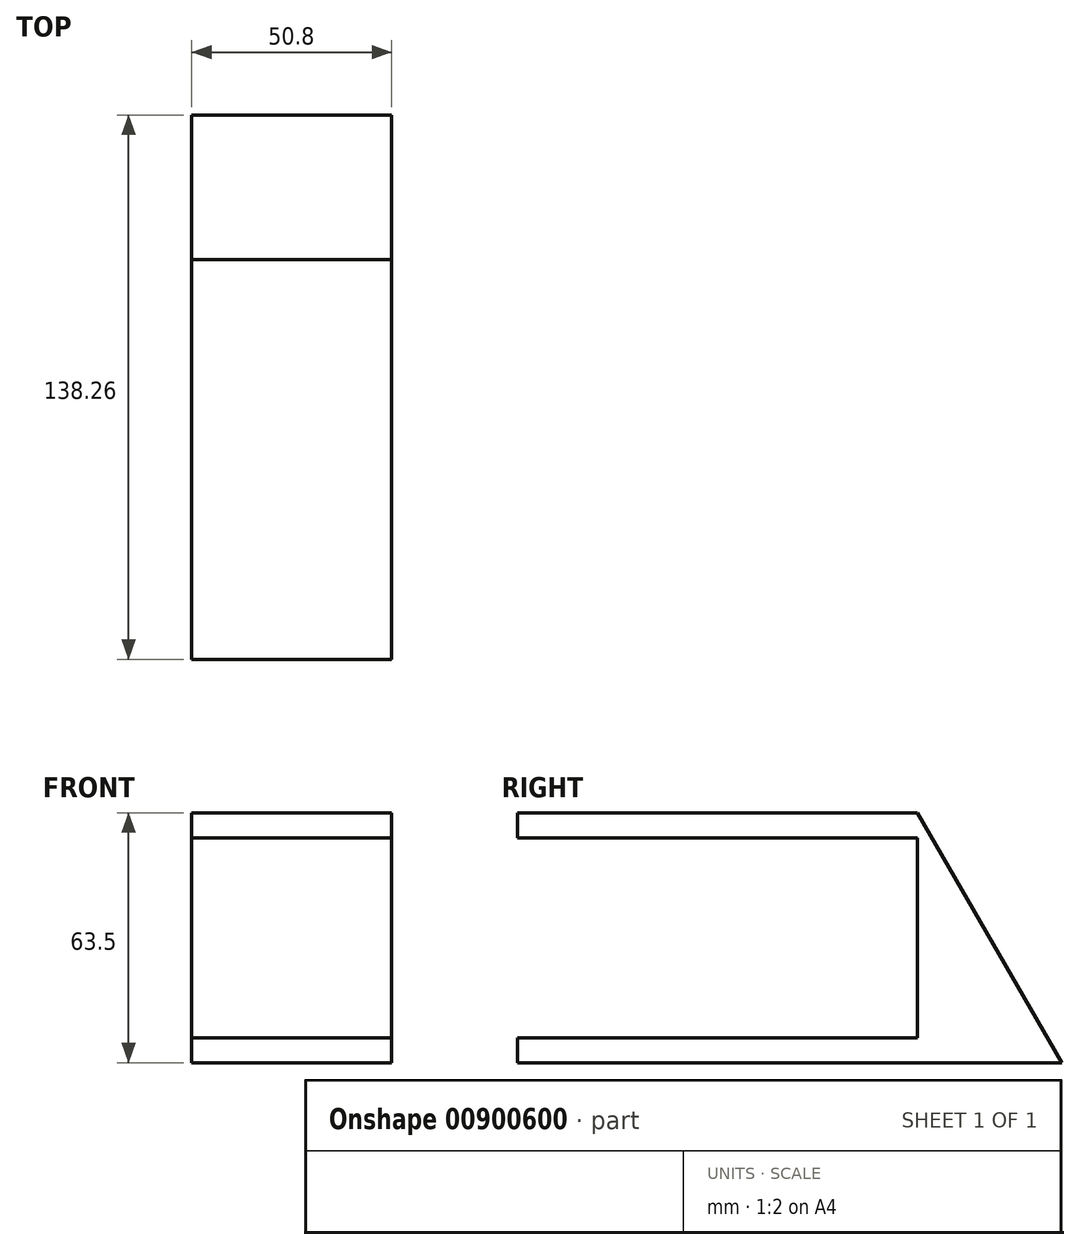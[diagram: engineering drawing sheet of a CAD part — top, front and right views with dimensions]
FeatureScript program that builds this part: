
annotation { "Feature Type Name" : "Feature", "Feature Type Description" : "" }
export const myFeature = defineFeature(function(context is Context, id is Id, definition is map)
    precondition{}
    {
        {
            var Q0;
            Q0=qCreatedBy(makeId("Right.planeOp"),FACE);
            var sketch = newSketch(context, id + "F0", { "sketchPlane" : qUnion([Q0])});
            skLineSegment(sketch, "E0", {"start": v(0, 0) * mm, "end": v(73.32, 0) * mm});
            skLineSegment(sketch, "E1", {"start": v(36.66, 0) * mm, "end": v(0, 0) * mm});
            skLineSegment(sketch, "E2", {"start": v(0, 0) * mm, "end": v(0, 57.15) * mm});
            skLineSegment(sketch, "E3", {"start": v(0, 0) * mm, "end": v(-101.6, 0) * mm});
            skLineSegment(sketch, "E4", {"start": v(-101.6, 0) * mm, "end": v(-101.6, 6.35) * mm});
            skLineSegment(sketch, "E5", {"start": v(-101.6, 6.35) * mm, "end": v(0, 6.35) * mm});
            skLineSegment(sketch, "E6", {"start": v(0, 57.15) * mm, "end": v(-101.6, 57.15) * mm});
            skLineSegment(sketch, "E7", {"start": v(-101.6, 57.15) * mm, "end": v(-101.6, 63.5) * mm});
            skLineSegment(sketch, "E8", {"start": v(-101.6, 63.5) * mm, "end": v(0, 63.5) * mm});
            skPoint(sketch, "E9.start.orphan", {"position": v(73.32, 23.1) * mm});
            skLineSegment(sketch, "E10", {"start": v(0, 63.5) * mm, "end": v(36.66, 0) * mm});
            skPoint(sketch, "E11.orphan", {"position": v(73.32, 63.5) * mm});
            skSolve(sketch);
        }
        {
            var Q0;
            Q0 = qSketchRegion(id + "F0", true);
            extrude(context, id + "F1", {"entities" : qUnion([Q0]), "depth" : 50.8 * mm, "offsetDistance" : 25.4 * mm});
        }
    });
